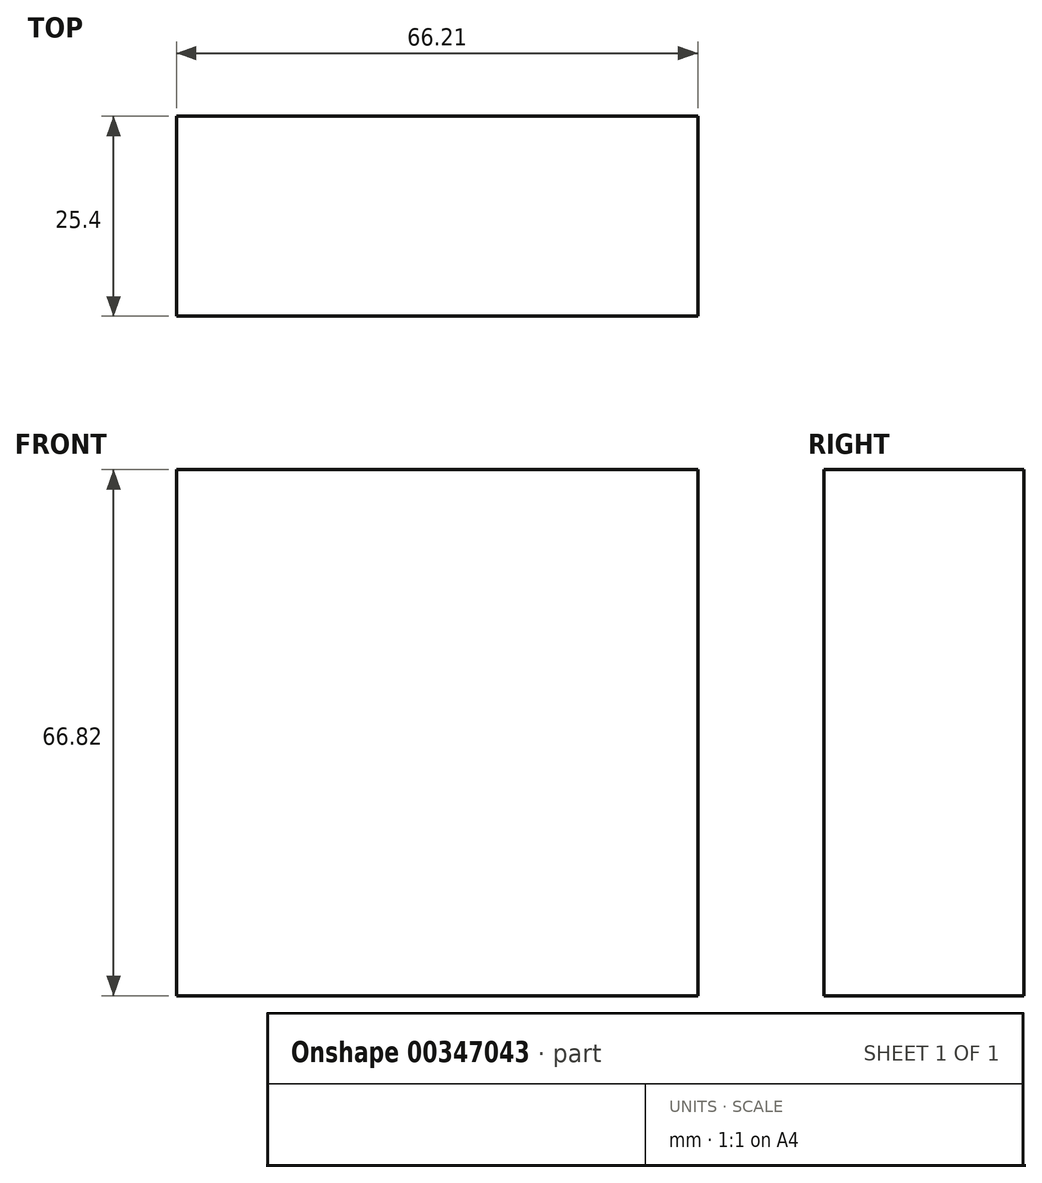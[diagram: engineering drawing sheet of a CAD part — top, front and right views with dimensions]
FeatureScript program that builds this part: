
annotation { "Feature Type Name" : "Feature", "Feature Type Description" : "" }
export const myFeature = defineFeature(function(context is Context, id is Id, definition is map)
    precondition{}
    {
        {
            var Q0;
            Q0=qCreatedBy(makeId("Front.planeOp"),FACE);
            var sketch = newSketch(context, id + "F0", { "sketchPlane" : qUnion([Q0])});
            skLineSegment(sketch, "E0.bottom", {"start": v(0, 0) * mm, "end": v(-66.21, 0) * mm});
            skLineSegment(sketch, "E0.top", {"start": v(0, -66.82) * mm, "end": v(-66.21, -66.82) * mm});
            skLineSegment(sketch, "E0.left", {"start": v(0, 0) * mm, "end": v(0, -66.82) * mm});
            skLineSegment(sketch, "E0.right", {"start": v(-66.21, 0) * mm, "end": v(-66.21, -66.82) * mm});
            skSolve(sketch);
        }
        {
            var Q0;
            Q0=makeQuery(id+"F0.imprint","IMPRINT",FACE,{"disambiguationData":[TD([[makeQuery(id+"F0.imprint","IMPRINT",EDGE,{"derivedFrom":sQuery(id+"F0.wireOp",EDGE,"E0.bottom")}),1.0]])]});
            extrude(context, id + "F1", {"entities" : qUnion([Q0]), "depth" : 25.4 * mm});
        }
    });
